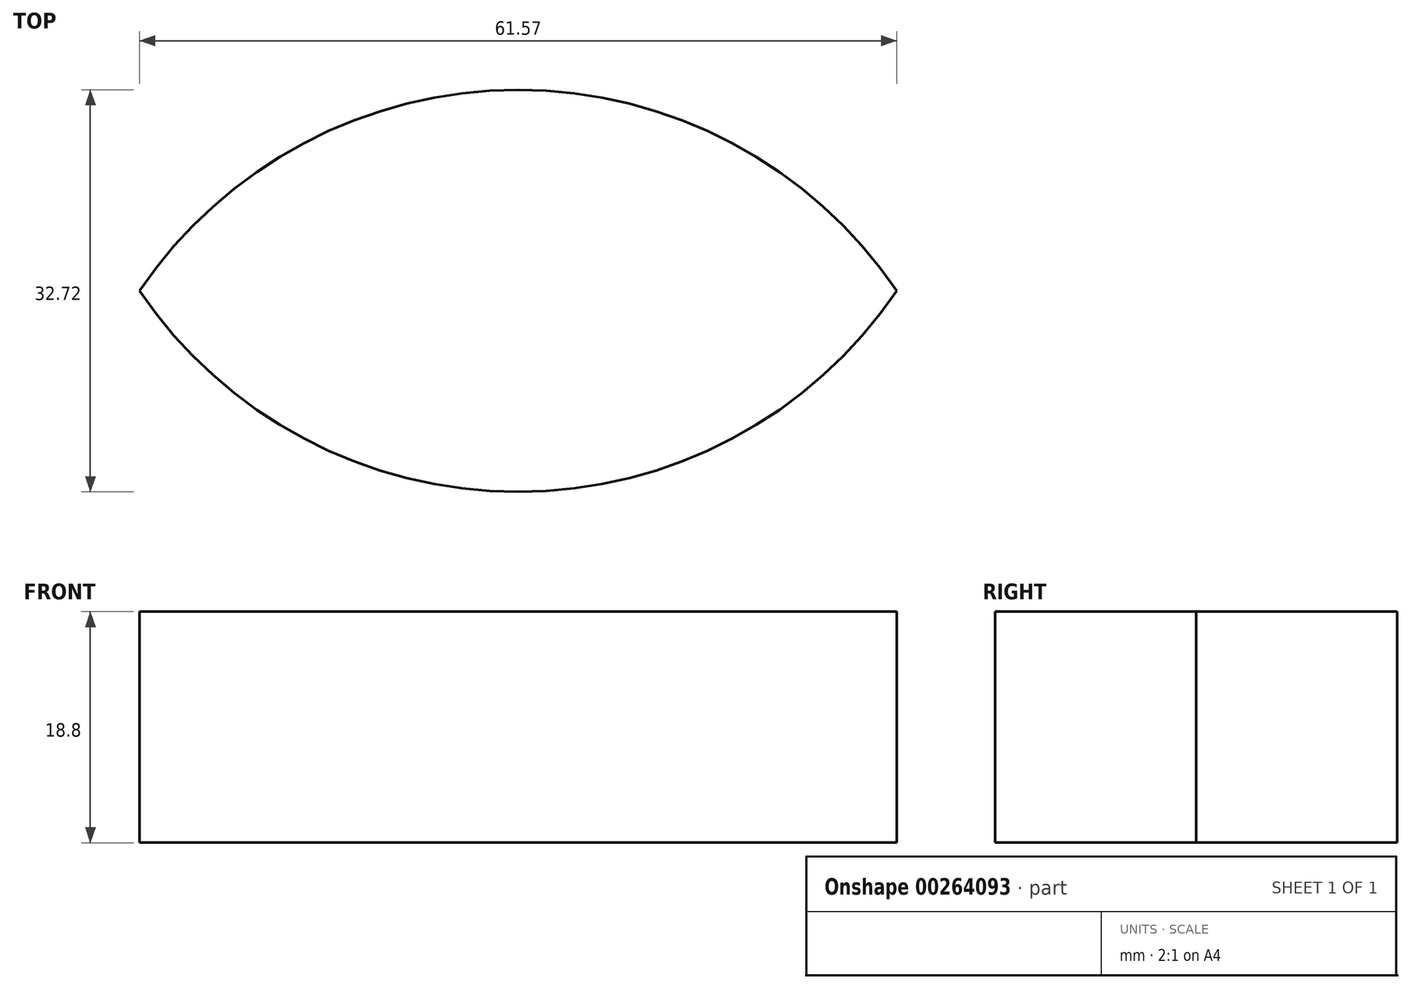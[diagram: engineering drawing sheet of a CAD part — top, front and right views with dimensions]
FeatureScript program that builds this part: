
annotation { "Feature Type Name" : "Feature", "Feature Type Description" : "" }
export const myFeature = defineFeature(function(context is Context, id is Id, definition is map)
    precondition{}
    {
        {
            var Q0;
            Q0=qCreatedBy(makeId("Top.planeOp"),FACE);
            var sketch = newSketch(context, id + "F0", { "sketchPlane" : qUnion([Q0])});
            skArc(sketch, "E0", {"start": v(0, 0) * mm, "mid": v(-30.79, 16.36) * mm, "end": v(-61.57, 0) * mm});
            skArc(sketch, "E1.MirrorCS", {"start": v(0, 0) * mm, "mid": v(-30.79, -16.36) * mm, "end": v(-61.57, 0) * mm});
            skSolve(sketch);
        }
        {
            var Q0;
            Q0=makeQuery(id+"F0.imprint","IMPRINT",FACE,{"disambiguationData":[TD([[makeQuery(id+"F0.imprint","IMPRINT",EDGE,{"derivedFrom":sQuery(id+"F0.wireOp",EDGE,"E0")}),1.0]])]});
            extrude(context, id + "F1", {"entities" : qUnion([Q0]), "oppositeDirection" : true, "depth" : 18.8 * mm});
        }
    });
